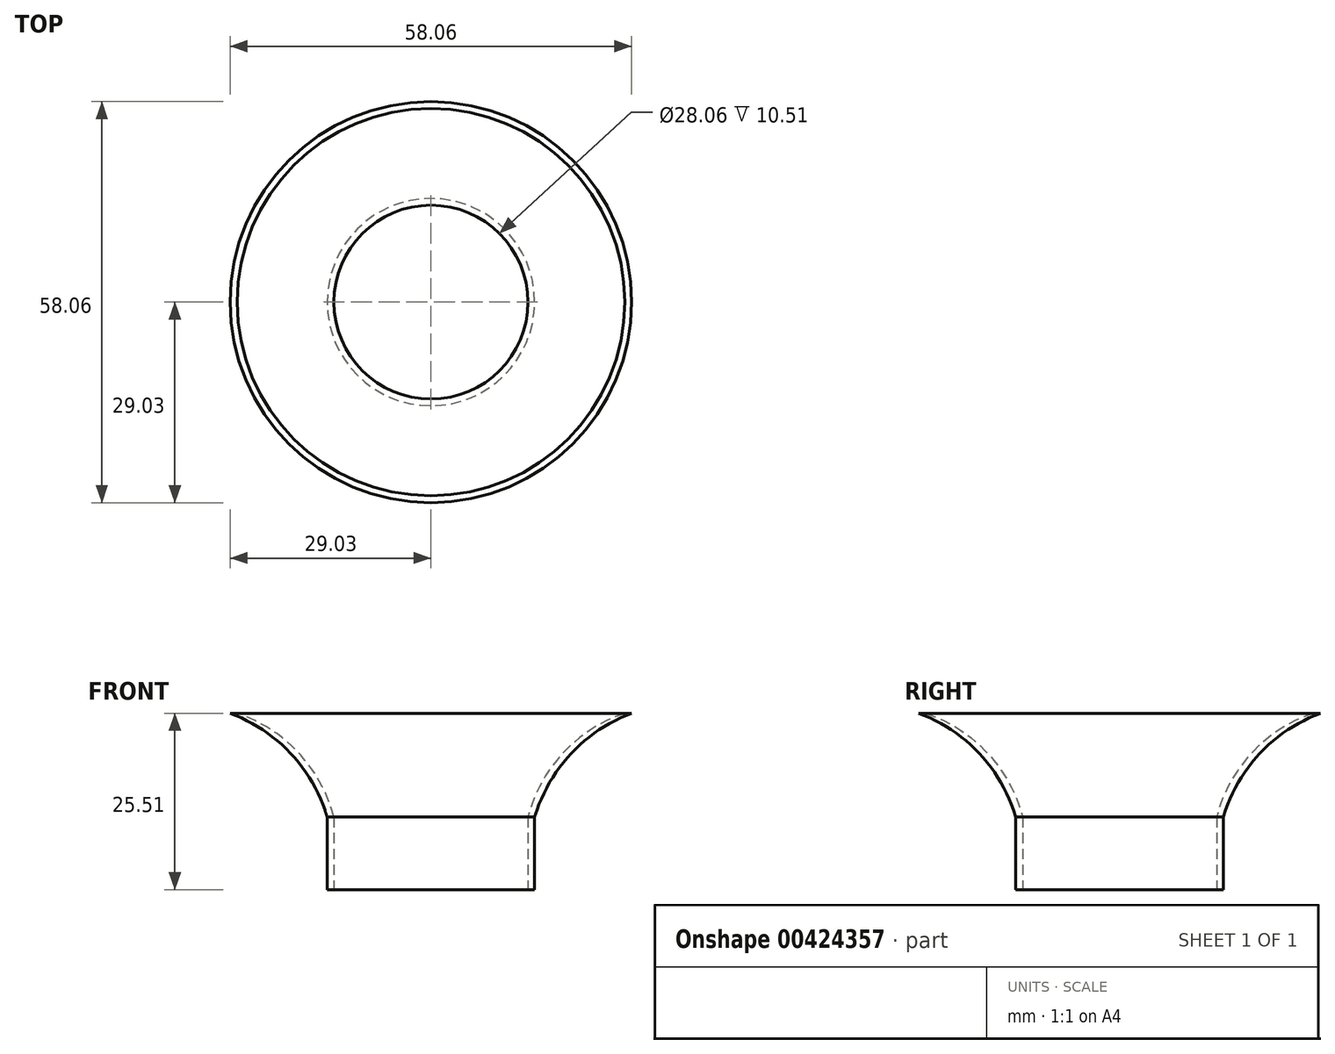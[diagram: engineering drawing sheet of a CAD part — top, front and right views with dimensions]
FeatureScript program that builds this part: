
annotation { "Feature Type Name" : "Feature", "Feature Type Description" : "" }
export const myFeature = defineFeature(function(context is Context, id is Id, definition is map)
    precondition{}
    {
        {
            var Q0;
            Q0=qCreatedBy(makeId("Front.planeOp"),FACE);
            var sketch = newSketch(context, id + "F0", { "sketchPlane" : qUnion([Q0])});
            skLineSegment(sketch, "E0", {"start": v(-14, 15) * mm, "end": v(-15, 15) * mm});
            skLineSegment(sketch, "E1", {"start": v(8.84, -17.89) * mm, "end": v(8.84, -17.89) * mm});
            skLineSegment(sketch, "E2", {"start": v(14.03, 0) * mm, "end": v(14.03, 15) * mm});
            skArc(sketch, "E3", {"start": v(-1.31, 1) * mm, "mid": v(-6.58, 9.54) * mm, "end": v(-15, 15) * mm});
            skArc(sketch, "E4", {"start": v(0, 0) * mm, "mid": v(-5.1, 9.28) * mm, "end": v(-14, 15) * mm});
            skLineSegment(sketch, "E5", {"start": v(-1.31, 1) * mm, "end": v(-0.97, 0) * mm});
            skLineSegment(sketch, "E6", {"start": v(-0.97, 0) * mm, "end": v(-0.97, -10.51) * mm});
            skLineSegment(sketch, "E7", {"start": v(-0.97, -10.51) * mm, "end": v(0, -10.51) * mm});
            skLineSegment(sketch, "E8", {"start": v(0, -10.51) * mm, "end": v(0, 0) * mm});
            skSolve(sketch);
        }
        {
            var Q0;
            Q0=makeQuery(id+"F0.imprint","IMPRINT",FACE,{"disambiguationData":[TD([[makeQuery(id+"F0.imprint","IMPRINT",EDGE,{"derivedFrom":sQuery(id+"F0.wireOp",EDGE,"E0")}),1.0]])]});
            var Q1;
            Q1=sQuery(id+"F0.wireOp",EDGE,"E2");
            revolve(context, id + "F1", {"entities" : qUnion([Q0]), "axis" : qUnion([Q1]), "revolveType" : RevolveType.FULL});
        }
    });
